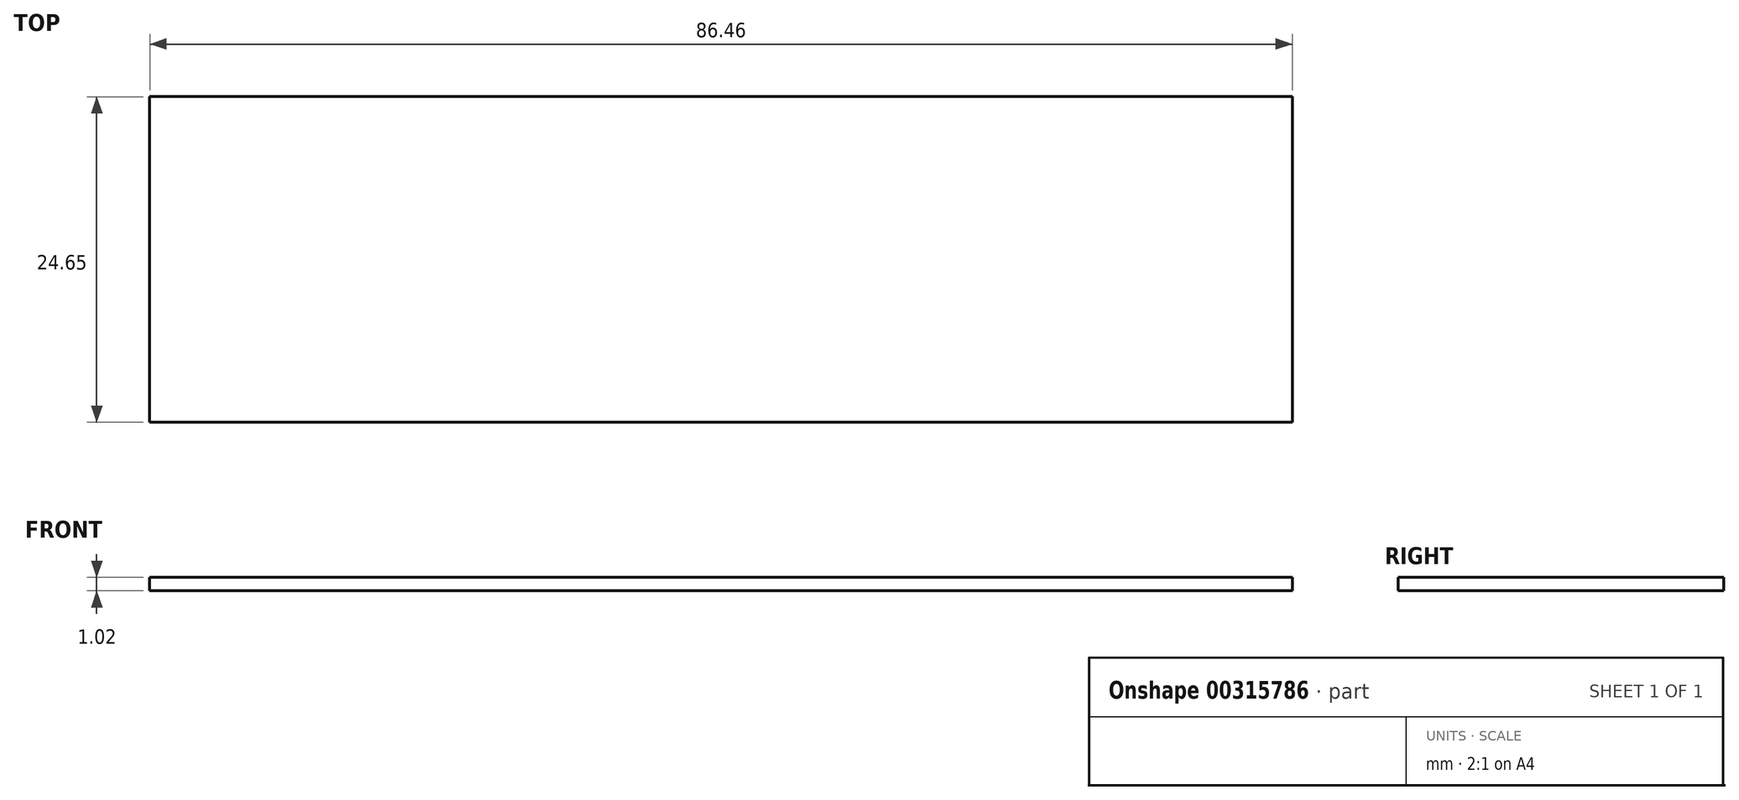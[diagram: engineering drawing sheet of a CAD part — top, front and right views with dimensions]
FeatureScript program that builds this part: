
annotation { "Feature Type Name" : "Feature", "Feature Type Description" : "" }
export const myFeature = defineFeature(function(context is Context, id is Id, definition is map)
    precondition{}
    {
        {
            var Q0;
            Q0=qCreatedBy(makeId("Top.planeOp"),FACE);
            var sketch = newSketch(context, id + "F0", { "sketchPlane" : qUnion([Q0])});
            skLineSegment(sketch, "E0.bottom", {"start": v(-38.46, 12.63) * mm, "end": v(48, 12.63) * mm});
            skLineSegment(sketch, "E0.top", {"start": v(-38.46, -12.02) * mm, "end": v(48, -12.02) * mm});
            skLineSegment(sketch, "E0.left", {"start": v(-38.46, 12.63) * mm, "end": v(-38.46, -12.02) * mm});
            skLineSegment(sketch, "E0.right", {"start": v(48, 12.63) * mm, "end": v(48, -12.02) * mm});
            skSolve(sketch);
        }
        {
            var Q0;
            Q0=makeQuery(id+"F0.imprint","IMPRINT",FACE,{"disambiguationData":[TD([[makeQuery(id+"F0.imprint","IMPRINT",EDGE,{"derivedFrom":sQuery(id+"F0.wireOp",EDGE,"E0.bottom")}),-1.0]])]});
            var Q1;
            Q1=makeQuery(id+"F0.imprint","IMPRINT",FACE,{"disambiguationData":[TD([[makeQuery(id+"F0.imprint","IMPRINT",EDGE,{"derivedFrom":sQuery(id+"F0.wireOp",EDGE,"E0.left")}),-1.0]])]});
            var Q2;
            Q2=makeQuery(id+"F0.imprint","IMPRINT",FACE,{"disambiguationData":[TD([[makeQuery(id+"F0.imprint","IMPRINT",EDGE,{"derivedFrom":sQuery(id+"F0.wireOp",EDGE,"E0.right")}),1.0]])]});
            extrude(context, id + "F1", {"entities" : qUnion([Q0, Q1, Q2]), "oppositeDirection" : true, "depth" : 1.02 * mm});
        }
    });
